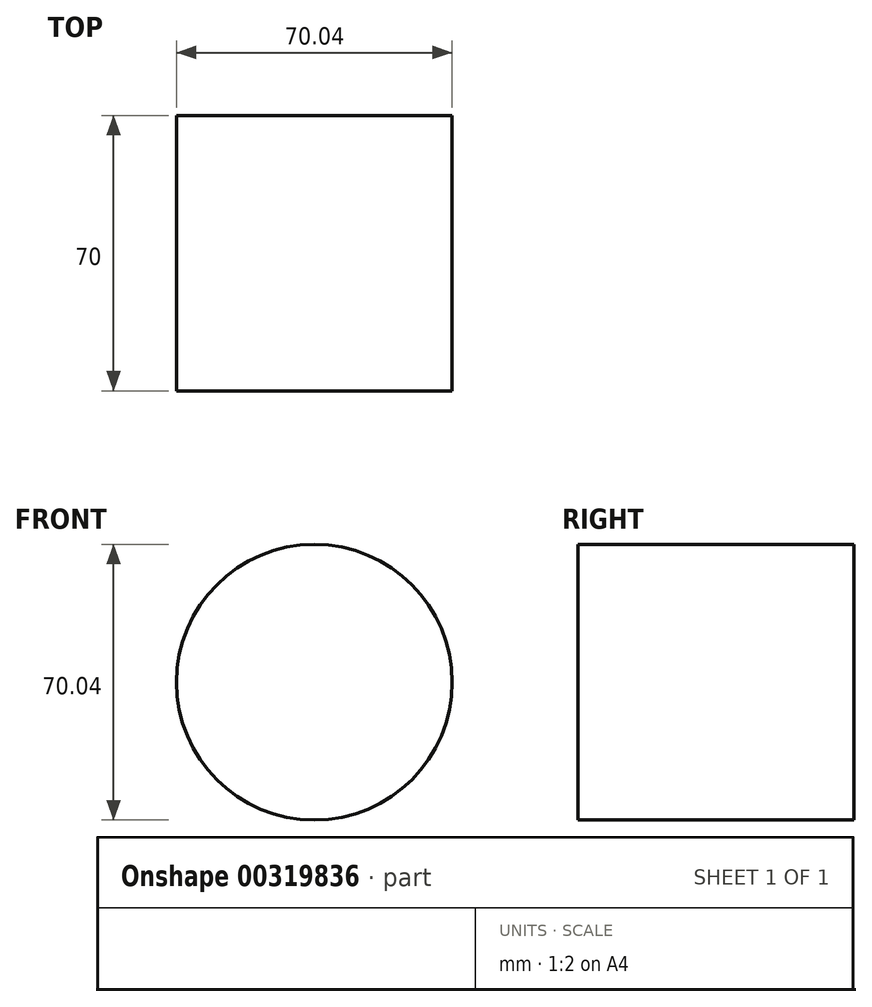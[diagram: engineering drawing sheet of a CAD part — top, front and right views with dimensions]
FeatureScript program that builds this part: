
annotation { "Feature Type Name" : "Feature", "Feature Type Description" : "" }
export const myFeature = defineFeature(function(context is Context, id is Id, definition is map)
    precondition{}
    {
        {
            var Q0;
            Q0=qCreatedBy(makeId("Front.planeOp"),FACE);
            var sketch = newSketch(context, id + "F0", { "sketchPlane" : qUnion([Q0])});
            skCircle(sketch, "E0", {"center": v(0, 0) * mm, "radius": 35.02 * mm});
            skSolve(sketch);
        }
        {
            var Q0;
            Q0 = qSketchRegion(id + "F0", true);
            extrude(context, id + "F1", {"entities" : qUnion([Q0]), "depth" : 70 * mm});
        }
    });
